# Revit family: Drinking_Fountain-Haws_Corporation-Wall_Mounted_1117.8 new new
name_source: partatom
category: Plumbing Fixtures
revit_build: Autodesk Revit Architecture 2015 (Build: 20160512_1515(x64)
units: mm (PartAtom-declared; Revit-internal decimal feet)

## types (1)
- H1117.8
    Amperage = 5 A
    Apparent Load = 582 VA
    Assembly Code = D2010810
    Back Plate = Metal - Haws Corporation - Satin Stainless Steel
    Basin Height = 0' - 4 1/4"
    Basin Width = 1' - 0"
    Beep Level = 0' - 3 19/32"
    Bowl = Metal - Haws Corporation - Satin Stainless Steel
    CW Connection = Yes
    CWFU = 2
    Cost = 0 $
    Cost Note = For Cost information please visit the Resource tab in the Product Page URL
    Default Elevation = 0' - 1 7/16"
    Description = Designed to run at a low energy usage, this water cooler and fountain are assured to have a long lasting life
    Flow = 0 GPM
    HW Connection = No
    HWFU = 0
    Keynote = 15410.A1
    Manufacturer = Haws Corporation
    Model = H1117.8
    Number of Poles = 1
    Power Consumption = 575 VA
    Power Factor = 0.987745
    Product Documentation Link = https://www.hawsco.com
    Product Page URL = https://www.hawsco.com
    Sanitary Radius = 0' - 0 5/8"
    Series = The Haws 1117 adjustable barrier free Hi-Lo drinking fountain
    Supply Radius = 0' - 0 3/16"
    Trim = Metal - Haws Corporation - Satin Stainless Steel
    Trim Plate = Yes
    Tubing = Metal - Haws Corporation - Copper Poly
    Type Comments = "Hi-Lo" electric drinking fountain with antimicrobial protection* provides 8 gph chilled water performance in an engineered stainless steel skin
    URL = http://www.hawsco.com
    Vent Connection = No
    Version = 2014-v2.0a
    Voltage = 115 V
    WFU = 1
    Waste Connection = Yes

## geometry (parser evidence)
native form markers: Blend x12, Sweep x11
no freeform markers — native parametric forms only
